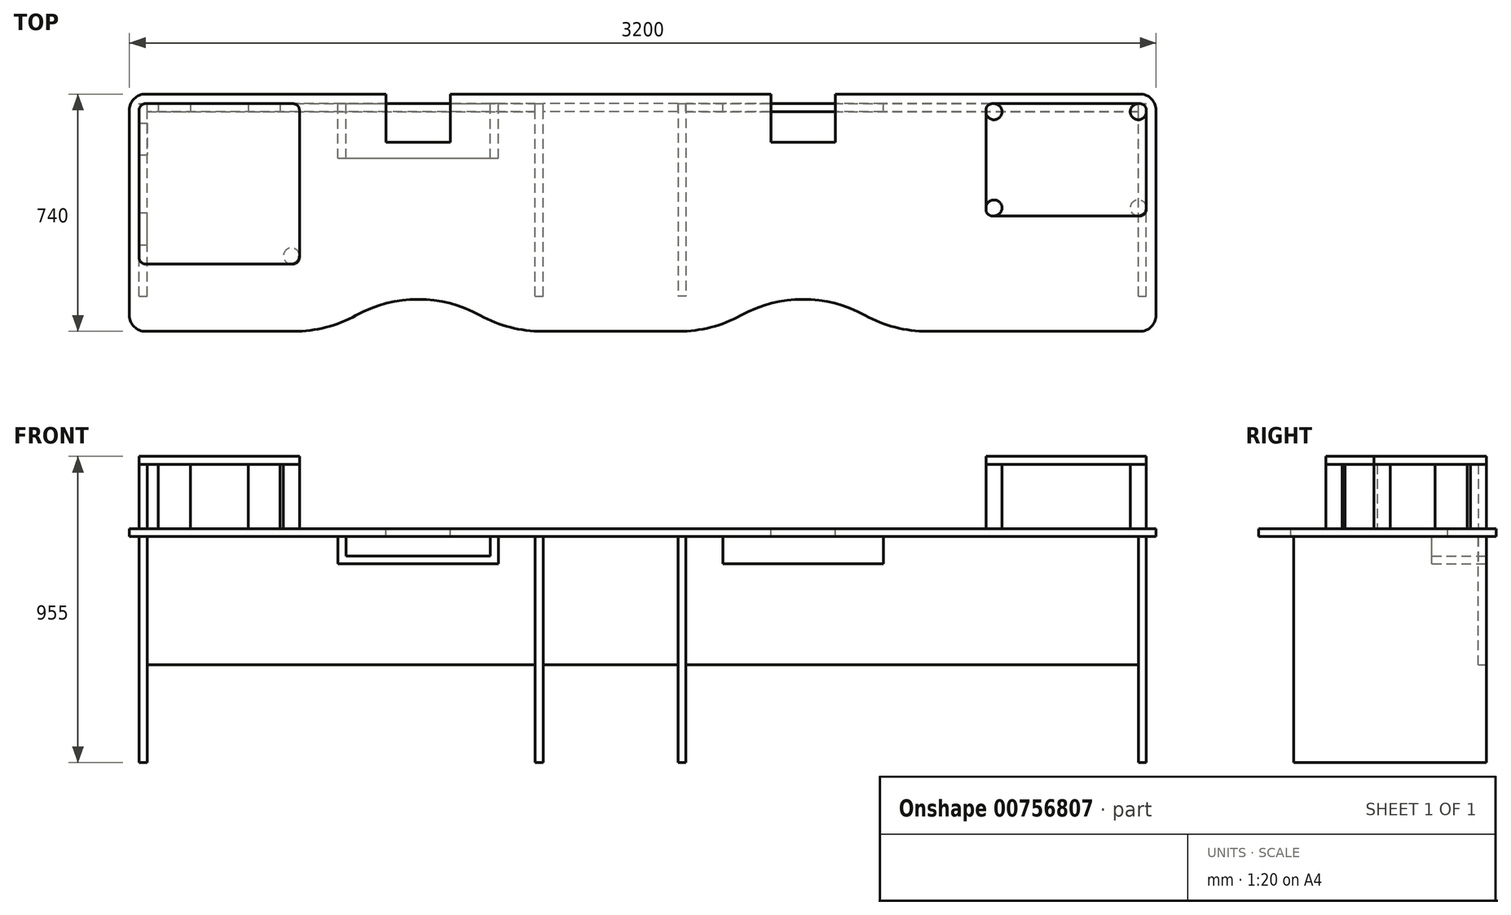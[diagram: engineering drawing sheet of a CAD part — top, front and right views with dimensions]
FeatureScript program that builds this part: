
annotation { "Feature Type Name" : "Feature", "Feature Type Description" : "" }
export const myFeature = defineFeature(function(context is Context, id is Id, definition is map)
    precondition{}
    {
        {
            var Q0;
            Q0=qCreatedBy(makeId("Top.planeOp"),FACE);
            var sketch = newSketch(context, id + "F0", { "sketchPlane" : qUnion([Q0])});
            skLineSegment(sketch, "E0.bottom", {"start": v(0, 0) * mm, "end": v(3200, 0) * mm, "construction": true});
            skLineSegment(sketch, "E0.top", {"start": v(0, -820) * mm, "end": v(3200, -820) * mm, "construction": true});
            skLineSegment(sketch, "E0.left", {"start": v(0, 0) * mm, "end": v(0, -820) * mm, "construction": true});
            skLineSegment(sketch, "E0.right", {"start": v(3200, 0) * mm, "end": v(3200, -820) * mm, "construction": true});
            skLineSegment(sketch, "E1", {"start": v(350, 0) * mm, "end": v(350, -820) * mm, "construction": true});
            skSolve(sketch);
        }
        {
            var Q0;
            Q0=qCreatedBy(makeId("Top.planeOp"),FACE);
            var sketch = newSketch(context, id + "F1", { "sketchPlane" : qUnion([Q0])});
            skLineSegment(sketch, "E2", {"start": v(0, 0) * mm, "end": v(800, 0) * mm});
            skLineSegment(sketch, "E3", {"start": v(800, 0) * mm, "end": v(800, -150) * mm});
            skLineSegment(sketch, "E4", {"start": v(800, -150) * mm, "end": v(1000, -150) * mm});
            skLineSegment(sketch, "E5", {"start": v(1000, -150) * mm, "end": v(1000, 0) * mm});
            skLineSegment(sketch, "E6", {"start": v(1000, 0) * mm, "end": v(2000, 0) * mm});
            skLineSegment(sketch, "E7", {"start": v(2000, 0) * mm, "end": v(2000, -150) * mm});
            skLineSegment(sketch, "E8", {"start": v(2000, -150) * mm, "end": v(2200, -150) * mm});
            skLineSegment(sketch, "E9", {"start": v(2200, -150) * mm, "end": v(2200, 0) * mm});
            skLineSegment(sketch, "E10", {"start": v(2200, 0) * mm, "end": v(3200, 0) * mm});
            skLineSegment(sketch, "E11", {"start": v(3200, 0) * mm, "end": v(3200, -740) * mm});
            skLineSegment(sketch, "E12", {"start": v(3200, -740) * mm, "end": v(2364.58, -740) * mm});
            skLineSegment(sketch, "E13", {"start": v(0, -740) * mm, "end": v(0, 0) * mm});
            skLineSegment(sketch, "E14", {"start": v(900, -150) * mm, "end": v(900, -740) * mm, "construction": true});
            skLineSegment(sketch, "E15", {"start": v(2100, -150) * mm, "end": v(2100, -740) * mm, "construction": true});
            skArc(sketch, "E16", {"start": v(1164.58, -740) * mm, "mid": v(900, -640) * mm, "end": v(635.42, -740) * mm});
            skArc(sketch, "E17", {"start": v(2364.58, -740) * mm, "mid": v(2100, -640) * mm, "end": v(1835.42, -740) * mm});
            skLineSegment(sketch, "E18.trimOffspring", {"start": v(635.42, -740) * mm, "end": v(0, -740) * mm});
            skLineSegment(sketch, "E19.trimOffspring", {"start": v(1835.42, -740) * mm, "end": v(1164.58, -740) * mm});
            skSolve(sketch);
        }
        {
            var Q0;
            Q0 = qSketchRegion(id + "F1", true);
            extrude(context, id + "F2", {"entities" : qUnion([Q0]), "oppositeDirection" : true, "depth" : 25 * mm, "offsetDistance" : 25 * mm});
        }
        {
            var Q0;
            Q0=makeQuery(id+"F2.opExtrude","SWEPT_EDGE",EDGE,{"disambiguationData":[OSD([sQuery(id+"F1.wireOp",EDGE,"E16"),sQuery(id+"F1.wireOp",EDGE,"E18.trimOffspring")])]});
            var Q1;
            Q1=makeQuery(id+"F2.opExtrude","SWEPT_EDGE",EDGE,{"disambiguationData":[OSD([sQuery(id+"F1.wireOp",EDGE,"E16"),sQuery(id+"F1.wireOp",EDGE,"E19.trimOffspring")])]});
            var Q2;
            Q2=makeQuery(id+"F2.opExtrude","SWEPT_EDGE",EDGE,{"disambiguationData":[OSD([sQuery(id+"F1.wireOp",EDGE,"E17"),sQuery(id+"F1.wireOp",EDGE,"E19.trimOffspring")])]});
            var Q3;
            Q3=makeQuery(id+"F2.opExtrude","SWEPT_EDGE",EDGE,{"disambiguationData":[OSD([sQuery(id+"F1.wireOp",EDGE,"E12"),sQuery(id+"F1.wireOp",EDGE,"E17")])]});
            fillet(context, id + "F3", {"entities" : qUnion([Q0, Q1, Q2, Q3]), "radius" : 400 * mm, "tangentPropagation" : true, "allowEdgeOverflow" : false});
        }
        {
            var Q0;
            Q0=makeQuery(id+"F2.opExtrude","CAP_EDGE",EDGE,{"disambiguationData":[OSD([sQuery(id+"F1.wireOp",EDGE,"E19.trimOffspring")])],"isStart":false});
            cPoint(context, id + "F4", {"entities" : qUnion([Q0]), "parameter" : 0.5});
        }
        {
            var Q0;
            Q0=qCreatedBy(makeId("Right.planeOp"),FACE);
            var Q1;
            Q1 = qCreatedBy(id + "F4" ,VERTEX);
            cPlane(context, id + "F5", {"entities" : qUnion([Q0, Q1]), "cplaneType" : CPlaneType.PLANE_POINT, "offset" : 25 * mm, "width" : 150 * mm, "height" : 150 * mm});
        }
        {
            var Q0;
            Q0=makeQuery(id+"F2.opExtrude","CAP_FACE",FACE,{"disambiguationData":[OSD([sQuery(id+"F1.wireOp",EDGE,"E2"),sQuery(id+"F1.wireOp",EDGE,"E3"),sQuery(id+"F1.wireOp",EDGE,"E4"),sQuery(id+"F1.wireOp",EDGE,"E5"),sQuery(id+"F1.wireOp",EDGE,"E6"),sQuery(id+"F1.wireOp",EDGE,"E7"),sQuery(id+"F1.wireOp",EDGE,"E8"),sQuery(id+"F1.wireOp",EDGE,"E9"),sQuery(id+"F1.wireOp",EDGE,"E10"),sQuery(id+"F1.wireOp",EDGE,"E11"),sQuery(id+"F1.wireOp",EDGE,"E12"),sQuery(id+"F1.wireOp",EDGE,"E13"),sQuery(id+"F1.wireOp",EDGE,"E16"),sQuery(id+"F1.wireOp",EDGE,"E17"),sQuery(id+"F1.wireOp",EDGE,"E18.trimOffspring"),sQuery(id+"F1.wireOp",EDGE,"E19.trimOffspring")])],"isStart":false});
            var sketch = newSketch(context, id + "F6", { "sketchPlane" : qUnion([Q0])});
            skLineSegment(sketch, "E20.bottom", {"start": v(1265, 630) * mm, "end": v(1290, 630) * mm});
            skLineSegment(sketch, "E20.top", {"start": v(1265, 0) * mm, "end": v(1290, 0) * mm});
            skLineSegment(sketch, "E20.left", {"start": v(1265, 630) * mm, "end": v(1265, 0) * mm});
            skLineSegment(sketch, "E20.right", {"start": v(1290, 630) * mm, "end": v(1290, 0) * mm});
            skLineSegment(sketch, "E21", {"start": v(1500, 740) * mm, "end": v(1500, 0) * mm, "construction": true});
            skLineSegment(sketch, "E22.bottom", {"start": v(1735, 0) * mm, "end": v(1710, 0) * mm});
            skLineSegment(sketch, "E22.top", {"start": v(1735, 630) * mm, "end": v(1710, 630) * mm});
            skLineSegment(sketch, "E22.left", {"start": v(1735, 0) * mm, "end": v(1735, 630) * mm});
            skLineSegment(sketch, "E22.right", {"start": v(1710, 0) * mm, "end": v(1710, 630) * mm});
            skLineSegment(sketch, "E23.bottom", {"start": v(30, 630) * mm, "end": v(55, 630) * mm});
            skLineSegment(sketch, "E23.top", {"start": v(30, 0) * mm, "end": v(55, 0) * mm});
            skLineSegment(sketch, "E23.left", {"start": v(30, 630) * mm, "end": v(30, 0) * mm});
            skLineSegment(sketch, "E23.right", {"start": v(55, 630) * mm, "end": v(55, 0) * mm});
            skLineSegment(sketch, "E24.bottom", {"start": v(3145, 630) * mm, "end": v(3170, 630) * mm});
            skLineSegment(sketch, "E24.top", {"start": v(3145, 0) * mm, "end": v(3170, 0) * mm});
            skLineSegment(sketch, "E24.left", {"start": v(3145, 630) * mm, "end": v(3145, 0) * mm});
            skLineSegment(sketch, "E24.right", {"start": v(3170, 630) * mm, "end": v(3170, 0) * mm});
            skSolve(sketch);
        }
        {
            var Q0;
            Q0 = qSketchRegion(id + "F6", true);
            extrude(context, id + "F7", {"entities" : qUnion([Q0]), "operationType" : NewBodyOperationType.ADD, "depth" : 705 * mm, "offsetDistance" : 25 * mm});
        }
        {
            var Q0;
            Q0=makeQuery(id+"F2.opExtrude","CAP_FACE",FACE,{"disambiguationData":[OSD([sQuery(id+"F1.wireOp",EDGE,"E2"),sQuery(id+"F1.wireOp",EDGE,"E3"),sQuery(id+"F1.wireOp",EDGE,"E4"),sQuery(id+"F1.wireOp",EDGE,"E5"),sQuery(id+"F1.wireOp",EDGE,"E6"),sQuery(id+"F1.wireOp",EDGE,"E7"),sQuery(id+"F1.wireOp",EDGE,"E8"),sQuery(id+"F1.wireOp",EDGE,"E9"),sQuery(id+"F1.wireOp",EDGE,"E10"),sQuery(id+"F1.wireOp",EDGE,"E11"),sQuery(id+"F1.wireOp",EDGE,"E12"),sQuery(id+"F1.wireOp",EDGE,"E13"),sQuery(id+"F1.wireOp",EDGE,"E16"),sQuery(id+"F1.wireOp",EDGE,"E17"),sQuery(id+"F1.wireOp",EDGE,"E18.trimOffspring"),sQuery(id+"F1.wireOp",EDGE,"E19.trimOffspring")])],"isStart":false});
            var sketch = newSketch(context, id + "F8", { "sketchPlane" : qUnion([Q0])});
            skLineSegment(sketch, "E25.bottom", {"start": v(650, 200) * mm, "end": v(675, 200) * mm});
            skLineSegment(sketch, "E25.top", {"start": v(650, 0) * mm, "end": v(675, 0) * mm});
            skLineSegment(sketch, "E25.left", {"start": v(650, 200) * mm, "end": v(650, 0) * mm});
            skLineSegment(sketch, "E25.right", {"start": v(675, 200) * mm, "end": v(675, 0) * mm});
            skLineSegment(sketch, "E26", {"start": v(900, 150) * mm, "end": v(900, 0) * mm, "construction": true});
            skLineSegment(sketch, "E27.bottom", {"start": v(1125, 200) * mm, "end": v(1150, 200) * mm});
            skLineSegment(sketch, "E27.top", {"start": v(1125, 0) * mm, "end": v(1150, 0) * mm});
            skLineSegment(sketch, "E27.left", {"start": v(1125, 200) * mm, "end": v(1125, 0) * mm});
            skLineSegment(sketch, "E27.right", {"start": v(1150, 200) * mm, "end": v(1150, 0) * mm});
            skSolve(sketch);
        }
        {
            var Q0;
            Q0 = qSketchRegion(id + "F8", true);
            extrude(context, id + "F9", {"entities" : qUnion([Q0]), "operationType" : NewBodyOperationType.ADD, "depth" : 60 * mm, "offsetDistance" : 25 * mm});
        }
        {
            var Q0;
            Q0=makeQuery(id+"F9.opExtrude","CAP_FACE",FACE,{"disambiguationData":[OSD([sQuery(id+"F8.wireOp",EDGE,"E25.bottom"),sQuery(id+"F8.wireOp",EDGE,"E25.top"),sQuery(id+"F8.wireOp",EDGE,"E25.left"),sQuery(id+"F8.wireOp",EDGE,"E25.right")])],"isStart":false});
            var sketch = newSketch(context, id + "F10", { "sketchPlane" : qUnion([Q0])});
            skLineSegment(sketch, "E28.bottom", {"start": v(650, 200) * mm, "end": v(1150, 200) * mm});
            skLineSegment(sketch, "E28.top", {"start": v(650, 0) * mm, "end": v(1150, 0) * mm});
            skLineSegment(sketch, "E28.left", {"start": v(650, 200) * mm, "end": v(650, 0) * mm});
            skLineSegment(sketch, "E28.right", {"start": v(1150, 200) * mm, "end": v(1150, 0) * mm});
            skSolve(sketch);
        }
        {
            var Q0;
            Q0 = qSketchRegion(id + "F10", true);
            extrude(context, id + "F11", {"entities" : qUnion([Q0]), "operationType" : NewBodyOperationType.ADD, "depth" : 25 * mm, "offsetDistance" : 25 * mm});
        }
        {
            var Q0;
            Q0=makeQuery(id+"F2.opExtrude","CAP_FACE",FACE,{"disambiguationData":[OSD([sQuery(id+"F1.wireOp",EDGE,"E2"),sQuery(id+"F1.wireOp",EDGE,"E3"),sQuery(id+"F1.wireOp",EDGE,"E4"),sQuery(id+"F1.wireOp",EDGE,"E5"),sQuery(id+"F1.wireOp",EDGE,"E6"),sQuery(id+"F1.wireOp",EDGE,"E7"),sQuery(id+"F1.wireOp",EDGE,"E8"),sQuery(id+"F1.wireOp",EDGE,"E9"),sQuery(id+"F1.wireOp",EDGE,"E10"),sQuery(id+"F1.wireOp",EDGE,"E11"),sQuery(id+"F1.wireOp",EDGE,"E12"),sQuery(id+"F1.wireOp",EDGE,"E13"),sQuery(id+"F1.wireOp",EDGE,"E16"),sQuery(id+"F1.wireOp",EDGE,"E17"),sQuery(id+"F1.wireOp",EDGE,"E18.trimOffspring"),sQuery(id+"F1.wireOp",EDGE,"E19.trimOffspring")])],"isStart":false});
            var sketch = newSketch(context, id + "F12", { "sketchPlane" : qUnion([Q0])});
            skLineSegment(sketch, "E29.bottom", {"start": v(3200, 0) * mm, "end": v(0, 0) * mm});
            skLineSegment(sketch, "E29.top", {"start": v(3200, 30) * mm, "end": v(0, 30) * mm});
            skLineSegment(sketch, "E29.left", {"start": v(3200, 0) * mm, "end": v(3200, 30) * mm});
            skLineSegment(sketch, "E29.right", {"start": v(0, 0) * mm, "end": v(0, 30) * mm});
            skSolve(sketch);
        }
        {
            var Q0;
            Q0 = qSketchRegion(id + "F12", true);
            extrude(context, id + "F13", {"entities" : qUnion([Q0]), "operationType" : NewBodyOperationType.REMOVE, "endBound" : BoundingType.THROUGH_ALL, "depth" : 25 * mm, "offsetDistance" : 25 * mm});
        }
        {
            var Q0;
            Q0=makeQuery(id+"F2.opExtrude","SWEPT_EDGE",EDGE,{"disambiguationData":[OSD([sQuery(id+"F1.wireOp",EDGE,"E11"),sQuery(id+"F1.wireOp",EDGE,"E12")])]});
            var Q1;
            Q1=makeQuery(id+"F2.opExtrude","SWEPT_EDGE",EDGE,{"disambiguationData":[OSD([sQuery(id+"F1.wireOp",EDGE,"E10"),sQuery(id+"F1.wireOp",EDGE,"E11")])]});
            var Q2;
            Q2=makeQuery(id+"F2.opExtrude","SWEPT_EDGE",EDGE,{"disambiguationData":[OSD([sQuery(id+"F1.wireOp",EDGE,"E2"),sQuery(id+"F1.wireOp",EDGE,"E13")])]});
            var Q3;
            Q3=makeQuery(id+"F2.opExtrude","SWEPT_EDGE",EDGE,{"disambiguationData":[OSD([sQuery(id+"F1.wireOp",EDGE,"E13"),sQuery(id+"F1.wireOp",EDGE,"E18.trimOffspring")])]});
            fillet(context, id + "F14", {"entities" : qUnion([Q0, Q1, Q2, Q3]), "radius" : 50 * mm, "tangentPropagation" : true, "allowEdgeOverflow" : false});
        }
        {
            var Q0;
            Q0=makeQuery(id+"F2.opExtrude","CAP_FACE",FACE,{"disambiguationData":[OSD([sQuery(id+"F1.wireOp",EDGE,"E2"),sQuery(id+"F1.wireOp",EDGE,"E3"),sQuery(id+"F1.wireOp",EDGE,"E4"),sQuery(id+"F1.wireOp",EDGE,"E5"),sQuery(id+"F1.wireOp",EDGE,"E6"),sQuery(id+"F1.wireOp",EDGE,"E7"),sQuery(id+"F1.wireOp",EDGE,"E8"),sQuery(id+"F1.wireOp",EDGE,"E9"),sQuery(id+"F1.wireOp",EDGE,"E10"),sQuery(id+"F1.wireOp",EDGE,"E11"),sQuery(id+"F1.wireOp",EDGE,"E12"),sQuery(id+"F1.wireOp",EDGE,"E13"),sQuery(id+"F1.wireOp",EDGE,"E16"),sQuery(id+"F1.wireOp",EDGE,"E17"),sQuery(id+"F1.wireOp",EDGE,"E18.trimOffspring"),sQuery(id+"F1.wireOp",EDGE,"E19.trimOffspring")])],"isStart":true});
            var sketch = newSketch(context, id + "F15", { "sketchPlane" : qUnion([Q0])});
            skLineSegment(sketch, "E30.bottom", {"start": v(30, -30) * mm, "end": v(530, -30) * mm, "construction": true});
            skLineSegment(sketch, "E30.top", {"start": v(30, -530) * mm, "end": v(530, -530) * mm, "construction": true});
            skLineSegment(sketch, "E30.left", {"start": v(30, -30) * mm, "end": v(30, -530) * mm, "construction": true});
            skLineSegment(sketch, "E30.right", {"start": v(530, -30) * mm, "end": v(530, -530) * mm, "construction": true});
            skLineSegment(sketch, "E31.bottom", {"start": v(90, -30) * mm, "end": v(190, -30) * mm});
            skLineSegment(sketch, "E31.top", {"start": v(90, -55) * mm, "end": v(190, -55) * mm});
            skLineSegment(sketch, "E31.left", {"start": v(90, -30) * mm, "end": v(90, -55) * mm});
            skLineSegment(sketch, "E31.right", {"start": v(190, -30) * mm, "end": v(190, -55) * mm});
            skLineSegment(sketch, "E32", {"start": v(280, -30) * mm, "end": v(280, -530) * mm, "construction": true});
            skLineSegment(sketch, "E33", {"start": v(530, -280) * mm, "end": v(30, -280) * mm, "construction": true});
            skLineSegment(sketch, "E34.bottom", {"start": v(30, -90) * mm, "end": v(55, -90) * mm});
            skLineSegment(sketch, "E34.top", {"start": v(30, -190) * mm, "end": v(55, -190) * mm});
            skLineSegment(sketch, "E34.left", {"start": v(30, -90) * mm, "end": v(30, -190) * mm});
            skLineSegment(sketch, "E34.right", {"start": v(55, -90) * mm, "end": v(55, -190) * mm});
            skLineSegment(sketch, "E35.bottom", {"start": v(370, -30) * mm, "end": v(470, -30) * mm});
            skLineSegment(sketch, "E35.top", {"start": v(370, -55) * mm, "end": v(470, -55) * mm});
            skLineSegment(sketch, "E35.left", {"start": v(370, -30) * mm, "end": v(370, -55) * mm});
            skLineSegment(sketch, "E35.right", {"start": v(470, -30) * mm, "end": v(470, -55) * mm});
            skLineSegment(sketch, "E36.bottom", {"start": v(30, -470) * mm, "end": v(55, -470) * mm});
            skLineSegment(sketch, "E36.top", {"start": v(30, -370) * mm, "end": v(55, -370) * mm});
            skLineSegment(sketch, "E36.left", {"start": v(30, -470) * mm, "end": v(30, -370) * mm});
            skLineSegment(sketch, "E36.right", {"start": v(55, -470) * mm, "end": v(55, -370) * mm});
            skCircle(sketch, "E37", {"center": v(505, -505) * mm, "radius": 25 * mm});
            skSolve(sketch);
        }
        {
            var Q0;
            Q0 = qSketchRegion(id + "F15", true);
            extrude(context, id + "F16", {"entities" : qUnion([Q0]), "depth" : 200 * mm, "offsetDistance" : 25 * mm});
        }
        {
            var Q0;
            Q0=makeQuery(id+"F16.opExtrude","CAP_FACE",FACE,{"disambiguationData":[OSD([sQuery(id+"F15.wireOp",EDGE,"E31.bottom"),sQuery(id+"F15.wireOp",EDGE,"E31.top"),sQuery(id+"F15.wireOp",EDGE,"E31.left"),sQuery(id+"F15.wireOp",EDGE,"E31.right")])],"isStart":false});
            var sketch = newSketch(context, id + "F17", { "sketchPlane" : qUnion([Q0])});
            skPoint(sketch, "E38.0", {"position": v(30, -30) * mm});
            skPoint(sketch, "E39.0", {"position": v(530, -530) * mm});
            skLineSegment(sketch, "E40.bottom", {"start": v(30, -30) * mm, "end": v(530, -30) * mm});
            skLineSegment(sketch, "E40.top", {"start": v(30, -530) * mm, "end": v(530, -530) * mm});
            skLineSegment(sketch, "E40.left", {"start": v(30, -30) * mm, "end": v(30, -530) * mm});
            skLineSegment(sketch, "E40.right", {"start": v(530, -30) * mm, "end": v(530, -530) * mm});
            skSolve(sketch);
        }
        {
            var Q0;
            Q0 = qSketchRegion(id + "F17", true);
            extrude(context, id + "F18", {"entities" : qUnion([Q0]), "depth" : 25 * mm, "offsetDistance" : 25 * mm});
        }
        {
            var Q0;
            Q0=makeQuery(id+"F18.opExtrude","SWEPT_EDGE",EDGE,{"disambiguationData":[OSD([sQuery(id+"F17.wireOp",EDGE,"E40.top"),sQuery(id+"F17.wireOp",EDGE,"E40.right")])]});
            var Q1;
            Q1=makeQuery(id+"F18.opExtrude","SWEPT_EDGE",EDGE,{"disambiguationData":[OSD([sQuery(id+"F17.wireOp",EDGE,"E40.bottom"),sQuery(id+"F17.wireOp",EDGE,"E40.right")])]});
            var Q2;
            Q2=makeQuery(id+"F18.opExtrude","SWEPT_EDGE",EDGE,{"disambiguationData":[OSD([sQuery(id+"F17.wireOp",EDGE,"E40.top"),sQuery(id+"F17.wireOp",EDGE,"E40.left")])]});
            var Q3;
            Q3=makeQuery(id+"F18.opExtrude","SWEPT_EDGE",EDGE,{"disambiguationData":[OSD([sQuery(id+"F17.wireOp",EDGE,"E40.bottom"),sQuery(id+"F17.wireOp",EDGE,"E40.left")])]});
            fillet(context, id + "F19", {"entities" : qUnion([Q0, Q1, Q2, Q3]), "radius" : 20 * mm, "tangentPropagation" : true, "allowEdgeOverflow" : false});
        }
        {
            var Q0;
            {var subQ1=sQuery(id+"F6.wireOp",EDGE,"E23.left");var subQ2=sQuery(id+"F12.wireOp",EDGE,"E29.top");Q0=makeQuery(id+"F13.boolean.opBoolean","COPY",FACE,{"disambiguationData":[TD([makeQuery(id+"F7.opExtrude","SWEPT_FACE",FACE,{"disambiguationData":[OSD([subQ1])]})])],"derivedFrom":makeQuery(id+"F13.opExtrude","SWEPT_FACE",FACE,{"disambiguationData":[OSD([subQ2])]})});}
            var sketch = newSketch(context, id + "F20", { "sketchPlane" : qUnion([Q0])});
            skLineSegment(sketch, "E41", {"start": v(-55, -425) * mm, "end": v(-55, -25) * mm});
            skLineSegment(sketch, "E42", {"start": v(-55, -25) * mm, "end": v(-650, -25) * mm});
            skLineSegment(sketch, "E43", {"start": v(-650, -25) * mm, "end": v(-650, -110) * mm});
            skLineSegment(sketch, "E44", {"start": v(-650, -110) * mm, "end": v(-1150, -110) * mm});
            skLineSegment(sketch, "E45", {"start": v(-1150, -110) * mm, "end": v(-1150, -25) * mm});
            skLineSegment(sketch, "E46", {"start": v(-1150, -25) * mm, "end": v(-1265, -25) * mm});
            skLineSegment(sketch, "E47", {"start": v(-1265, -25) * mm, "end": v(-1265, -425) * mm});
            skLineSegment(sketch, "E48", {"start": v(-1265, -425) * mm, "end": v(-55, -425) * mm});
            skLineSegment(sketch, "E49", {"start": v(-1710, -25) * mm, "end": v(-1290, -25) * mm});
            skLineSegment(sketch, "E50", {"start": v(-1290, -25) * mm, "end": v(-1290, -425) * mm});
            skLineSegment(sketch, "E51", {"start": v(-1290, -425) * mm, "end": v(-1710, -425) * mm});
            skLineSegment(sketch, "E52", {"start": v(-1710, -425) * mm, "end": v(-1710, -25) * mm});
            skLineSegment(sketch, "E53", {"start": v(-3145, -25) * mm, "end": v(-2350, -25) * mm});
            skLineSegment(sketch, "E54", {"start": v(-2350, -25) * mm, "end": v(-2350, -110) * mm});
            skLineSegment(sketch, "E55", {"start": v(-2350, -110) * mm, "end": v(-1850, -110) * mm});
            skLineSegment(sketch, "E56", {"start": v(-1850, -110) * mm, "end": v(-1850, -25) * mm});
            skLineSegment(sketch, "E57", {"start": v(-1850, -25) * mm, "end": v(-1735, -25) * mm});
            skLineSegment(sketch, "E58", {"start": v(-1735, -25) * mm, "end": v(-1735, -425) * mm});
            skLineSegment(sketch, "E59", {"start": v(-1735, -425) * mm, "end": v(-3145, -425) * mm});
            skLineSegment(sketch, "E60", {"start": v(-3145, -425) * mm, "end": v(-3145, -25) * mm});
            skSolve(sketch);
        }
        {
            var Q0;
            Q0 = qSketchRegion(id + "F20", true);
            extrude(context, id + "F21", {"entities" : qUnion([Q0]), "oppositeDirection" : true, "depth" : 25 * mm, "offsetDistance" : 25 * mm});
        }
        {
            var Q0;
            Q0=makeQuery(id+"F2.opExtrude","CAP_FACE",FACE,{"disambiguationData":[OSD([sQuery(id+"F1.wireOp",EDGE,"E2"),sQuery(id+"F1.wireOp",EDGE,"E3"),sQuery(id+"F1.wireOp",EDGE,"E4"),sQuery(id+"F1.wireOp",EDGE,"E5"),sQuery(id+"F1.wireOp",EDGE,"E6"),sQuery(id+"F1.wireOp",EDGE,"E7"),sQuery(id+"F1.wireOp",EDGE,"E8"),sQuery(id+"F1.wireOp",EDGE,"E9"),sQuery(id+"F1.wireOp",EDGE,"E10"),sQuery(id+"F1.wireOp",EDGE,"E11"),sQuery(id+"F1.wireOp",EDGE,"E12"),sQuery(id+"F1.wireOp",EDGE,"E13"),sQuery(id+"F1.wireOp",EDGE,"E16"),sQuery(id+"F1.wireOp",EDGE,"E17"),sQuery(id+"F1.wireOp",EDGE,"E18.trimOffspring"),sQuery(id+"F1.wireOp",EDGE,"E19.trimOffspring")])],"isStart":true});
            var sketch = newSketch(context, id + "F22", { "sketchPlane" : qUnion([Q0])});
            skLineSegment(sketch, "E61.bottom", {"start": v(2670, -30) * mm, "end": v(3170, -30) * mm, "construction": true});
            skLineSegment(sketch, "E61.top", {"start": v(2670, -380) * mm, "end": v(3170, -380) * mm, "construction": true});
            skLineSegment(sketch, "E61.left", {"start": v(2670, -30) * mm, "end": v(2670, -380) * mm, "construction": true});
            skLineSegment(sketch, "E61.right", {"start": v(3170, -30) * mm, "end": v(3170, -380) * mm, "construction": true});
            skCircle(sketch, "E62", {"center": v(2695, -55) * mm, "radius": 25 * mm});
            skCircle(sketch, "E63", {"center": v(3145, -55) * mm, "radius": 25 * mm});
            skCircle(sketch, "E64", {"center": v(3145, -355) * mm, "radius": 25 * mm});
            skCircle(sketch, "E65", {"center": v(2695, -355) * mm, "radius": 25 * mm});
            skSolve(sketch);
        }
        {
            var Q0;
            Q0 = qSketchRegion(id + "F22", true);
            extrude(context, id + "F23", {"entities" : qUnion([Q0]), "depth" : 200 * mm, "offsetDistance" : 25 * mm});
        }
        {
            var Q0;
            Q0=makeQuery(id+"F23.opExtrude","CAP_FACE",FACE,{"disambiguationData":[OSD([sQuery(id+"F22.wireOp",EDGE,"E63")])],"isStart":false});
            var sketch = newSketch(context, id + "F24", { "sketchPlane" : qUnion([Q0])});
            skPoint(sketch, "E66.0", {"position": v(2670, -30) * mm});
            skPoint(sketch, "E67.0", {"position": v(3170, -380) * mm});
            skLineSegment(sketch, "E68.bottom", {"start": v(2670, -30) * mm, "end": v(3170, -30) * mm});
            skLineSegment(sketch, "E68.top", {"start": v(2670, -380) * mm, "end": v(3170, -380) * mm});
            skLineSegment(sketch, "E68.left", {"start": v(2670, -30) * mm, "end": v(2670, -380) * mm});
            skLineSegment(sketch, "E68.right", {"start": v(3170, -30) * mm, "end": v(3170, -380) * mm});
            skSolve(sketch);
        }
        {
            var Q0;
            Q0 = qSketchRegion(id + "F24", true);
            extrude(context, id + "F25", {"entities" : qUnion([Q0]), "depth" : 25 * mm, "offsetDistance" : 25 * mm});
        }
        {
            var Q0;
            Q0=makeQuery(id+"F25.opExtrude","SWEPT_EDGE",EDGE,{"disambiguationData":[OSD([sQuery(id+"F24.wireOp",EDGE,"E68.top"),sQuery(id+"F24.wireOp",EDGE,"E68.left")])]});
            var Q1;
            Q1=makeQuery(id+"F25.opExtrude","SWEPT_EDGE",EDGE,{"disambiguationData":[OSD([sQuery(id+"F24.wireOp",EDGE,"E68.top"),sQuery(id+"F24.wireOp",EDGE,"E68.right")])]});
            var Q2;
            Q2=makeQuery(id+"F25.opExtrude","SWEPT_EDGE",EDGE,{"disambiguationData":[OSD([sQuery(id+"F24.wireOp",EDGE,"E68.bottom"),sQuery(id+"F24.wireOp",EDGE,"E68.left")])]});
            var Q3;
            Q3=makeQuery(id+"F25.opExtrude","SWEPT_EDGE",EDGE,{"disambiguationData":[OSD([sQuery(id+"F24.wireOp",EDGE,"E68.bottom"),sQuery(id+"F24.wireOp",EDGE,"E68.right")])]});
            fillet(context, id + "F26", {"entities" : qUnion([Q0, Q1, Q2, Q3]), "radius" : 20 * mm, "tangentPropagation" : true, "allowEdgeOverflow" : false});
        }
    });
